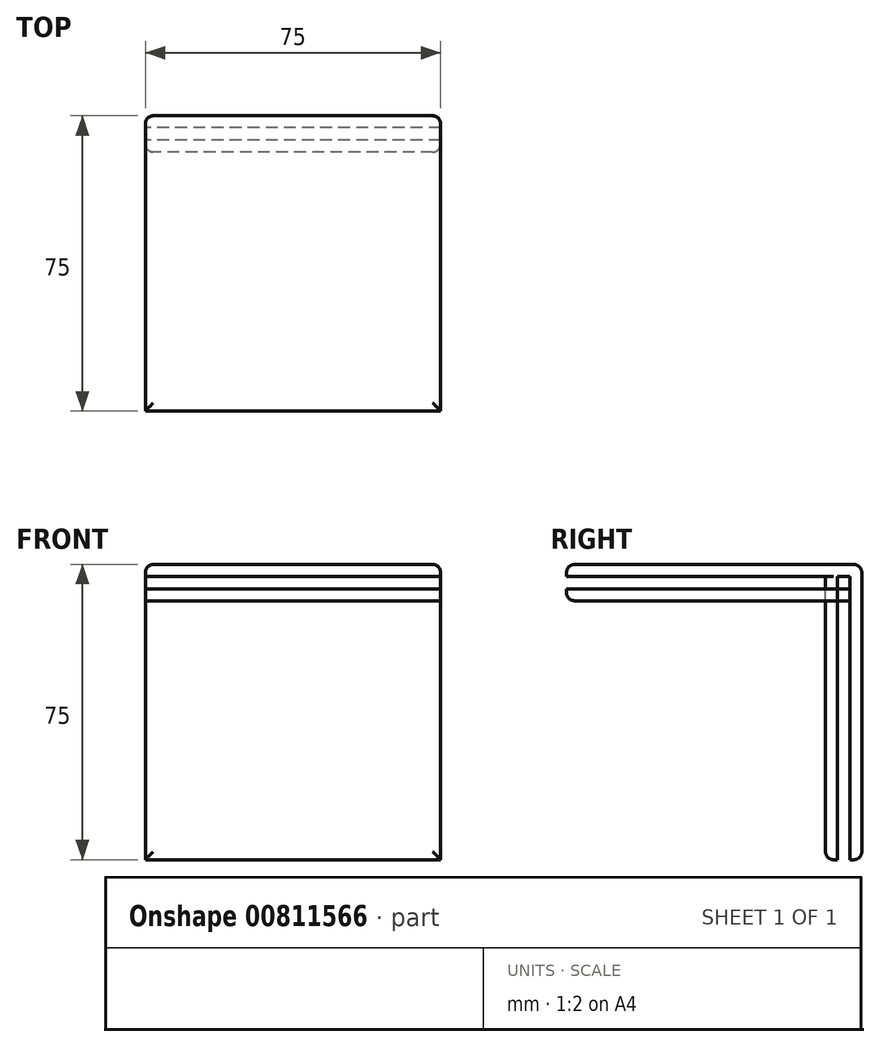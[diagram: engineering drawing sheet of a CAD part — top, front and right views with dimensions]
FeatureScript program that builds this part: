
annotation { "Feature Type Name" : "Feature", "Feature Type Description" : "" }
export const myFeature = defineFeature(function(context is Context, id is Id, definition is map)
    precondition{}
    {
        {
            var Q0;
            Q0=qCreatedBy(makeId("Top.planeOp"),FACE);
            var sketch = newSketch(context, id + "F0", { "sketchPlane" : qUnion([Q0])});
            skLineSegment(sketch, "E0.bottom", {"start": v(37.5, -37.5) * mm, "end": v(-37.5, -37.5) * mm});
            skLineSegment(sketch, "E0.top", {"start": v(37.5, 37.5) * mm, "end": v(-37.5, 37.5) * mm});
            skLineSegment(sketch, "E0.left", {"start": v(37.5, -37.5) * mm, "end": v(37.5, 37.5) * mm});
            skLineSegment(sketch, "E0.right", {"start": v(-37.5, -37.5) * mm, "end": v(-37.5, 37.5) * mm});
            skPoint(sketch, "E0.middle", {"position": v(0, 0) * mm});
            skSolve(sketch);
        }
        {
            var Q0;
            Q0 = qSketchRegion(id + "F0", true);
            extrude(context, id + "F1", {"entities" : qUnion([Q0]), "depth" : 3 * mm, "offsetDistance" : 25 * mm});
        }
        {
            var Q0;
            Q0=makeQuery(id+"F1.opExtrude","SWEPT_FACE",FACE,{"disambiguationData":[OSD([sQuery(id+"F0.wireOp",EDGE,"E0.right")])]});
            var sketch = newSketch(context, id + "F2", { "sketchPlane" : qUnion([Q0])});
            skLineSegment(sketch, "E1.bottom", {"start": v(-37.5, 3) * mm, "end": v(-34.5, 3) * mm});
            skLineSegment(sketch, "E1.top", {"start": v(-37.5, -72) * mm, "end": v(-34.5, -72) * mm});
            skLineSegment(sketch, "E1.left", {"start": v(-37.5, 3) * mm, "end": v(-37.5, -72) * mm});
            skLineSegment(sketch, "E1.right", {"start": v(-34.5, 3) * mm, "end": v(-34.5, -72) * mm});
            skLineSegment(sketch, "E2.bottom", {"start": v(-31.3, 3) * mm, "end": v(-28.3, 3) * mm});
            skLineSegment(sketch, "E2.top", {"start": v(-31.3, -72) * mm, "end": v(-28.3, -72) * mm});
            skLineSegment(sketch, "E2.left", {"start": v(-31.3, 3) * mm, "end": v(-31.3, -72) * mm});
            skLineSegment(sketch, "E2.right", {"start": v(-28.3, 3) * mm, "end": v(-28.3, -72) * mm});
            skLineSegment(sketch, "E3", {"start": v(-36, -72) * mm, "end": v(-7.39, -72) * mm, "construction": true});
            skSolve(sketch);
        }
        {
            var Q0;
            Q0 = qSketchRegion(id + "F2", true);
            var Q1;
            Q1=makeQuery(id+"F1.opExtrude","SWEPT_FACE",FACE,{"disambiguationData":[OSD([sQuery(id+"F0.wireOp",EDGE,"E0.left")])]});
            extrude(context, id + "F3", {"entities" : qUnion([Q0]), "operationType" : NewBodyOperationType.ADD, "endBound" : BoundingType.UP_TO_SURFACE, "oppositeDirection" : true, "depth" : 25 * mm, "endBoundEntityFace" : qUnion([Q1]), "offsetDistance" : 25 * mm});
        }
        {
            var Q0;
            Q0=makeQuery(id+"F1.opExtrude","SWEPT_FACE",FACE,{"disambiguationData":[OSD([sQuery(id+"F0.wireOp",EDGE,"E0.bottom")])]});
            var sketch = newSketch(context, id + "F4", { "sketchPlane" : qUnion([Q0])});
            skLineSegment(sketch, "E4.0", {"start": v(37.5, -3.2) * mm, "end": v(-37.5, -3.2) * mm});
            skLineSegment(sketch, "E5.bottom", {"start": v(-37.5, -3.2) * mm, "end": v(37.5, -3.2) * mm});
            skLineSegment(sketch, "E5.top", {"start": v(-37.5, -6.2) * mm, "end": v(37.5, -6.2) * mm});
            skLineSegment(sketch, "E5.left", {"start": v(-37.5, -3.2) * mm, "end": v(-37.5, -6.2) * mm});
            skLineSegment(sketch, "E5.right", {"start": v(37.5, -3.2) * mm, "end": v(37.5, -6.2) * mm});
            skLineSegment(sketch, "E6.0", {"start": v(37.5, -72) * mm, "end": v(37.5, -3.2) * mm});
            skSolve(sketch);
        }
        {
            var Q0;
            Q0 = qSketchRegion(id + "F4", true);
            var Q1;
            Q1=makeQuery(id+"F3.opExtrude","SWEPT_FACE",FACE,{"disambiguationData":[OSD([sQuery(id+"F2.wireOp",EDGE,"E1.right")])]});
            extrude(context, id + "F5", {"entities" : qUnion([Q0]), "endBound" : BoundingType.UP_TO_SURFACE, "oppositeDirection" : true, "depth" : 25 * mm, "endBoundEntityFace" : qUnion([Q1]), "offsetDistance" : 25 * mm});
        }
        {
            var Q0;
            Q0=makeQuery(id+"F3.boolean.opBoolean","MERGE",FACE,{"derivedFrom":[makeQuery(id+"F1.opExtrude","SWEPT_FACE",FACE,{"disambiguationData":[OSD([sQuery(id+"F0.wireOp",EDGE,"E0.right")])]}),makeQuery(id+"F3.opExtrude","CAP_FACE",FACE,{"disambiguationData":[OSD([sQuery(id+"F2.wireOp",EDGE,"E1.bottom"),sQuery(id+"F2.wireOp",EDGE,"E1.top"),sQuery(id+"F2.wireOp",EDGE,"E1.left"),sQuery(id+"F2.wireOp",EDGE,"E1.right")])],"isStart":true}),makeQuery(id+"F3.opExtrude","CAP_FACE",FACE,{"disambiguationData":[OSD([sQuery(id+"F2.wireOp",EDGE,"E2.bottom"),sQuery(id+"F2.wireOp",EDGE,"E2.top"),sQuery(id+"F2.wireOp",EDGE,"E2.left"),sQuery(id+"F2.wireOp",EDGE,"E2.right")])],"isStart":true})]});
            var sketch = newSketch(context, id + "F6", { "sketchPlane" : qUnion([Q0])});
            skLineSegment(sketch, "E7.0", {"start": v(-34.5, -3.2) * mm, "end": v(37.5, -3.2) * mm});
            skLineSegment(sketch, "E8.bottom", {"start": v(-34.5, 0) * mm, "end": v(-31.3, 0) * mm});
            skLineSegment(sketch, "E8.top", {"start": v(-34.5, -3.2) * mm, "end": v(-31.3, -3.2) * mm});
            skLineSegment(sketch, "E8.left", {"start": v(-34.5, 0) * mm, "end": v(-34.5, -3.2) * mm});
            skLineSegment(sketch, "E8.right", {"start": v(-31.3, 0) * mm, "end": v(-31.3, -3.2) * mm});
            skSolve(sketch);
        }
        {
            var Q0;
            Q0 = qSketchRegion(id + "F6", true);
            var Q1;
            Q1=makeQuery(id+"F3.boolean.opBoolean","MERGE",FACE,{"derivedFrom":[makeQuery(id+"F1.opExtrude","SWEPT_FACE",FACE,{"disambiguationData":[OSD([sQuery(id+"F0.wireOp",EDGE,"E0.left")])]}),makeQuery(id+"F3.opExtrude","CAP_FACE",FACE,{"disambiguationData":[OSD([sQuery(id+"F2.wireOp",EDGE,"E1.bottom"),sQuery(id+"F2.wireOp",EDGE,"E1.top"),sQuery(id+"F2.wireOp",EDGE,"E1.left"),sQuery(id+"F2.wireOp",EDGE,"E1.right")])],"isStart":false}),makeQuery(id+"F3.opExtrude","CAP_FACE",FACE,{"disambiguationData":[OSD([sQuery(id+"F2.wireOp",EDGE,"E2.bottom"),sQuery(id+"F2.wireOp",EDGE,"E2.top"),sQuery(id+"F2.wireOp",EDGE,"E2.left"),sQuery(id+"F2.wireOp",EDGE,"E2.right")])],"isStart":false})]});
            extrude(context, id + "F7", {"entities" : qUnion([Q0]), "endBound" : BoundingType.UP_TO_SURFACE, "oppositeDirection" : true, "depth" : 25 * mm, "endBoundEntityFace" : qUnion([Q1]), "offsetDistance" : 25 * mm});
        }
        {
            var Q0;
            Q0=makeQuery(id+"F1.opExtrude","CAP_FACE",FACE,{"disambiguationData":[OSD([sQuery(id+"F0.wireOp",EDGE,"E0.bottom"),sQuery(id+"F0.wireOp",EDGE,"E0.top"),sQuery(id+"F0.wireOp",EDGE,"E0.left"),sQuery(id+"F0.wireOp",EDGE,"E0.right")])],"isStart":false});
            var Q1;
            Q1=makeQuery(id+"F3.boolean.opBoolean","MERGE",FACE,{"derivedFrom":[makeQuery(id+"F1.opExtrude","SWEPT_FACE",FACE,{"disambiguationData":[OSD([sQuery(id+"F0.wireOp",EDGE,"E0.top")])]}),makeQuery(id+"F3.opExtrude","SWEPT_FACE",FACE,{"disambiguationData":[OSD([sQuery(id+"F2.wireOp",EDGE,"E1.left")])]})]});
            var Q2;
            Q2=makeQuery(id+"F5.opExtrude","CAP_EDGE",EDGE,{"disambiguationData":[OSD([sQuery(id+"F4.wireOp",EDGE,"E5.top")])],"isStart":true});
            var Q3;
            Q3=makeQuery(id+"F3.opExtrude","SWEPT_EDGE",EDGE,{"disambiguationData":[OSD([sQuery(id+"F2.wireOp",EDGE,"E2.top"),sQuery(id+"F2.wireOp",EDGE,"E2.right")])]});
            var Q4;
            Q4=makeQuery(id+"F3.opExtrude","CAP_EDGE",EDGE,{"disambiguationData":[OSD([sQuery(id+"F2.wireOp",EDGE,"E2.right")])],"isStart":false});
            var Q5;
            Q5=makeQuery(id+"F3.opExtrude","CAP_EDGE",EDGE,{"disambiguationData":[OSD([sQuery(id+"F2.wireOp",EDGE,"E2.right")])],"isStart":true});
            fillet(context, id + "F8", {"entities" : qUnion([Q0, Q1, Q2, Q3, Q4, Q5]), "radius" : 2 * mm, "tangentPropagation" : true, "allowEdgeOverflow" : false});
        }
    });
